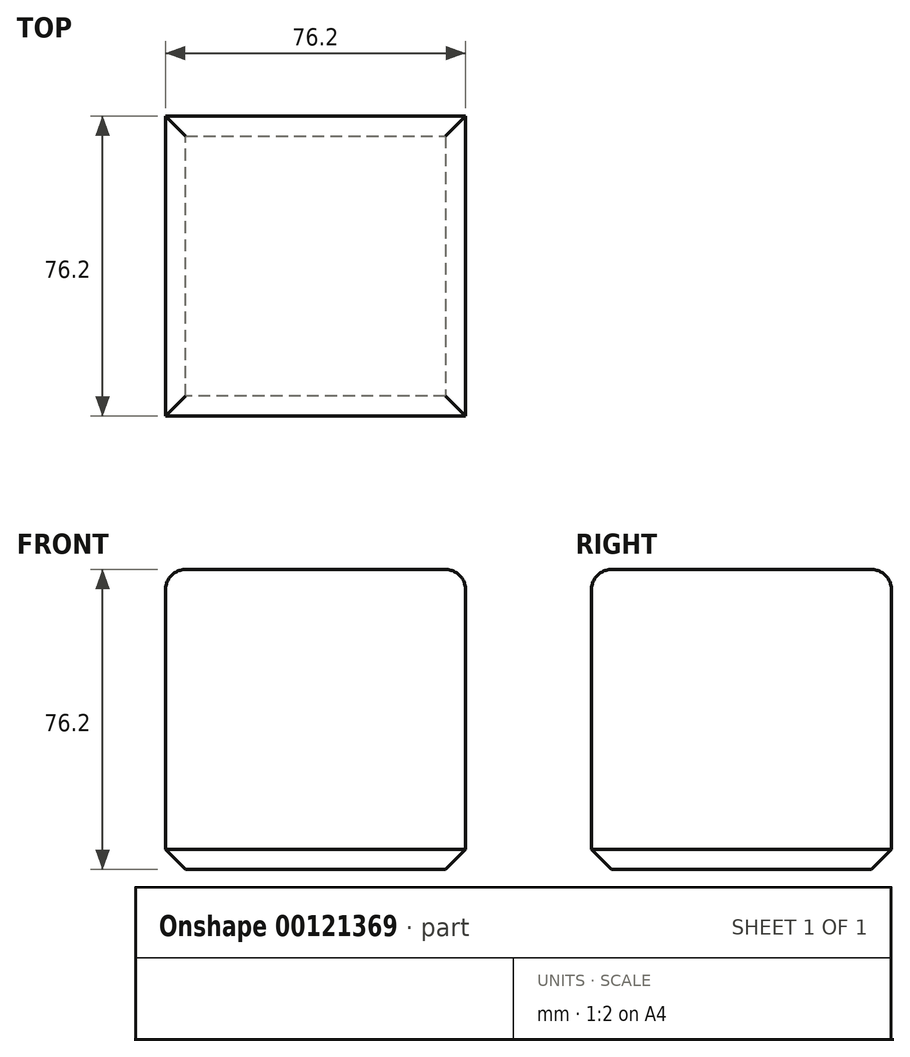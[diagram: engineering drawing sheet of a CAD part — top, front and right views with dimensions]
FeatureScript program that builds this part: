
annotation { "Feature Type Name" : "Feature", "Feature Type Description" : "" }
export const myFeature = defineFeature(function(context is Context, id is Id, definition is map)
    precondition{}
    {
        {
            var Q0;
            Q0=qCreatedBy(makeId("Front.planeOp"),FACE);
            var sketch = newSketch(context, id + "F0", { "sketchPlane" : qUnion([Q0])});
            skLineSegment(sketch, "E0.bottom", {"start": v(0, 0) * mm, "end": v(76.2, 0) * mm});
            skLineSegment(sketch, "E0.top", {"start": v(0, 76.2) * mm, "end": v(76.2, 76.2) * mm});
            skLineSegment(sketch, "E0.left", {"start": v(0, 0) * mm, "end": v(0, 76.2) * mm});
            skLineSegment(sketch, "E0.right", {"start": v(76.2, 0) * mm, "end": v(76.2, 76.2) * mm});
            skSolve(sketch);
        }
        {
            var Q0;
            Q0=makeQuery(id+"F0.imprint","IMPRINT",FACE,{"disambiguationData":[TD([[makeQuery(id+"F0.imprint","IMPRINT",EDGE,{"derivedFrom":sQuery(id+"F0.wireOp",EDGE,"E0.bottom")}),1.0]])]});
            extrude(context, id + "F1", {"entities" : qUnion([Q0]), "depth" : 76.2 * mm});
        }
        {
            var Q0;
            Q0=makeQuery(id+"F1.opExtrude","SWEPT_FACE",FACE,{"disambiguationData":[OSD([sQuery(id+"F0.wireOp",EDGE,"E0.top")])]});
            fillet(context, id + "F2", {"entities" : qUnion([Q0]), "radius" : 5.08 * mm, "tangentPropagation" : true, "allowEdgeOverflow" : false});
        }
        {
            var Q0;
            Q0=makeQuery(id+"F1.opExtrude","SWEPT_FACE",FACE,{"disambiguationData":[OSD([sQuery(id+"F0.wireOp",EDGE,"E0.bottom")])]});
            chamfer(context, id + "F3", {"entities" : qUnion([Q0]), "width" : 5.08 * mm, "tangentPropagation" : true});
        }
    });
